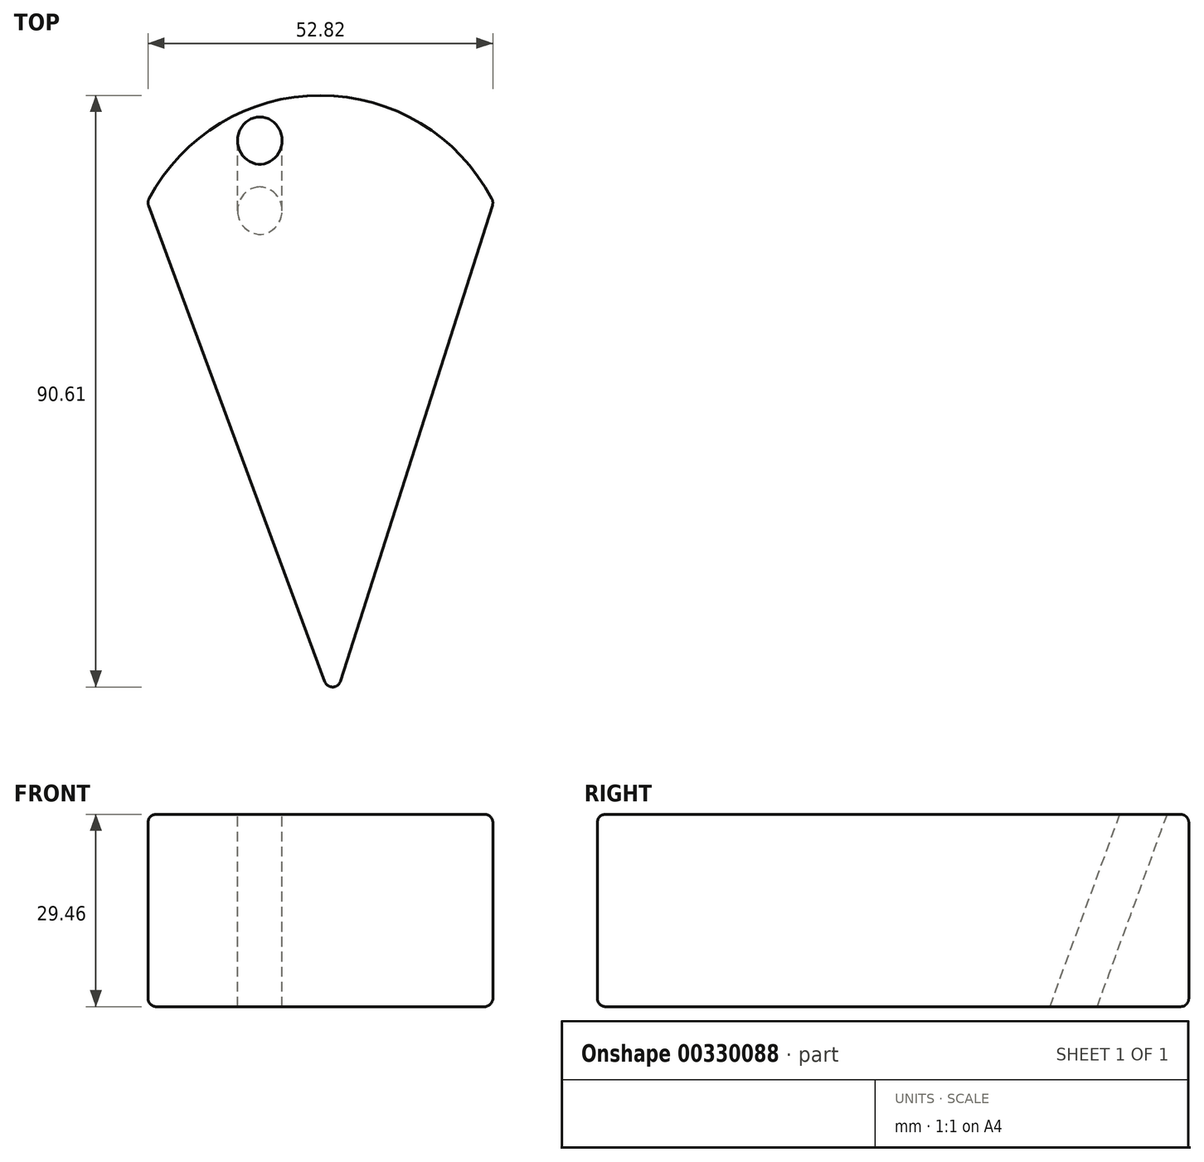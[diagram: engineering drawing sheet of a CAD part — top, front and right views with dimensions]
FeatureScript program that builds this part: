
annotation { "Feature Type Name" : "Feature", "Feature Type Description" : "" }
export const myFeature = defineFeature(function(context is Context, id is Id, definition is map)
    precondition{}
    {
        {
            var Q0;
            Q0=qCreatedBy(makeId("Top.planeOp"),FACE);
            var sketch = newSketch(context, id + "F0", { "sketchPlane" : qUnion([Q0])});
            skLineSegment(sketch, "E0", {"start": v(0, -40.98) * mm, "end": v(-28.47, 35.93) * mm});
            skLineSegment(sketch, "E1", {"start": v(0, -40.98) * mm, "end": v(24.57, 35.93) * mm});
            skArc(sketch, "E2", {"start": v(24.57, 35.93) * mm, "mid": v(-1.95, 52.26) * mm, "end": v(-28.47, 35.93) * mm});
            skSolve(sketch);
        }
        {
            var Q0;
            Q0=makeQuery(id+"F0.imprint","IMPRINT",FACE,{"disambiguationData":[TD([[makeQuery(id+"F0.imprint","IMPRINT",EDGE,{"derivedFrom":sQuery(id+"F0.wireOp",EDGE,"E0")}),-1.0]])]});
            extrude(context, id + "F1", {"entities" : qUnion([Q0]), "depth" : 29.46 * mm});
        }
        {
            var Q0;
            Q0=makeQuery(id+"F1.opExtrude","SWEPT_EDGE",EDGE,{"disambiguationData":[OSD([sQuery(id+"F0.wireOp",EDGE,"E0"),sQuery(id+"F0.wireOp",EDGE,"E1")])]});
            var Q1;
            Q1=makeQuery(id+"F1.opExtrude","CAP_EDGE",EDGE,{"disambiguationData":[OSD([sQuery(id+"F0.wireOp",EDGE,"E0")])],"isStart":true});
            var Q2;
            Q2=makeQuery(id+"F1.opExtrude","CAP_EDGE",EDGE,{"disambiguationData":[OSD([sQuery(id+"F0.wireOp",EDGE,"E0")])],"isStart":false});
            var Q3;
            Q3=makeQuery(id+"F1.opExtrude","CAP_EDGE",EDGE,{"disambiguationData":[OSD([sQuery(id+"F0.wireOp",EDGE,"E1")])],"isStart":true});
            var Q4;
            Q4=makeQuery(id+"F1.opExtrude","CAP_EDGE",EDGE,{"disambiguationData":[OSD([sQuery(id+"F0.wireOp",EDGE,"E1")])],"isStart":false});
            var Q5;
            Q5=makeQuery(id+"F1.opExtrude","CAP_EDGE",EDGE,{"disambiguationData":[OSD([sQuery(id+"F0.wireOp",EDGE,"E2")])],"isStart":false});
            var Q6;
            Q6=makeQuery(id+"F1.opExtrude","SWEPT_EDGE",EDGE,{"disambiguationData":[OSD([sQuery(id+"F0.wireOp",EDGE,"E1"),sQuery(id+"F0.wireOp",EDGE,"E2")])]});
            var Q7;
            Q7=makeQuery(id+"F1.opExtrude","SWEPT_EDGE",EDGE,{"disambiguationData":[OSD([sQuery(id+"F0.wireOp",EDGE,"E0"),sQuery(id+"F0.wireOp",EDGE,"E2")])]});
            var Q8;
            Q8=makeQuery(id+"F1.opExtrude","CAP_EDGE",EDGE,{"disambiguationData":[OSD([sQuery(id+"F0.wireOp",EDGE,"E2")])],"isStart":true});
            fillet(context, id + "F2", {"entities" : qUnion([Q0, Q1, Q2, Q3, Q4, Q5, Q6, Q7, Q8]), "radius" : 1.27 * mm, "tangentPropagation" : true, "allowEdgeOverflow" : false});
        }
        {
            var Q0;
            Q0=qCreatedBy(makeId("Top.planeOp"),FACE);
            var sketch = newSketch(context, id + "F3", { "sketchPlane" : qUnion([Q0])});
            skLineSegment(sketch, "E3", {"start": v(-86.44, 2.68) * mm, "end": v(114.81, 2.68) * mm, "construction": true});
            skSolve(sketch);
        }
        {
            var Q0;
            Q0=makeQuery(id+"F1.opExtrude","CAP_FACE",FACE,{"disambiguationData":[OSD([sQuery(id+"F0.wireOp",EDGE,"E0"),sQuery(id+"F0.wireOp",EDGE,"E1"),sQuery(id+"F0.wireOp",EDGE,"E2")])],"isStart":false});
            var Q1;
            Q1=sQuery(id+"F3.wireOp",EDGE,"E3");
            cPlane(context, id + "F4", {"entities" : qUnion([Q0, Q1]), "cplaneType" : CPlaneType.LINE_ANGLE, "offset" : 43.18 * mm, "angle" : 20 * degree, "oppositeDirection" : true, "width" : 152.4 * mm, "height" : 152.4 * mm});
        }
        {
            var Q0;
            Q0=qCreatedBy(id+"F4.planeOp",FACE);
            var sketch = newSketch(context, id + "F5", { "sketchPlane" : qUnion([Q0])});
            skCircle(sketch, "E4", {"center": v(-11.23, -32.53) * mm, "radius": 3.4 * mm});
            skSolve(sketch);
        }
        {
            var Q0;
            Q0=makeQuery(id+"F5.imprint","IMPRINT",FACE,{"disambiguationData":[TD([[makeQuery(id+"F5.imprint","IMPRINT",EDGE,{"derivedFrom":sQuery(id+"F5.wireOp",EDGE,"E4")}),1.0]])]});
            extrude(context, id + "F6", {"entities" : qUnion([Q0]), "operationType" : NewBodyOperationType.REMOVE, "endBound" : BoundingType.SYMMETRIC, "depth" : 139.7 * mm});
        }
    });
